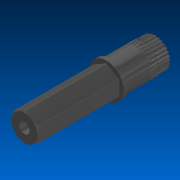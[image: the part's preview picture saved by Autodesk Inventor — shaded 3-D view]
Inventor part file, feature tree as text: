
AUTODESK INVENTOR PART (.ipt)
format: ipt  version: 2022.2 (Build 262287000, 287)  size: 1,431,552 bytes
history: native  units: in
note: dims shown in document units (in); Inventor stores cm internally (conversion verified against a paired STEP export)
features: fillet x1
ambient origin geometry x8: Origin, YZ Plane, XZ Plane, XY Plane, X Axis, Y Axis, Z Axis, Center Point
bodies: Solid1 (feature_tree)
feature tree (1):
  fillet  "Fillet5"  [1 undecoded]
note: 1 required parameter value undecoded (feature->parameter linkage not recoverable at this tier; creation-order binding heuristic only, values carry confidence <= 0.55)
